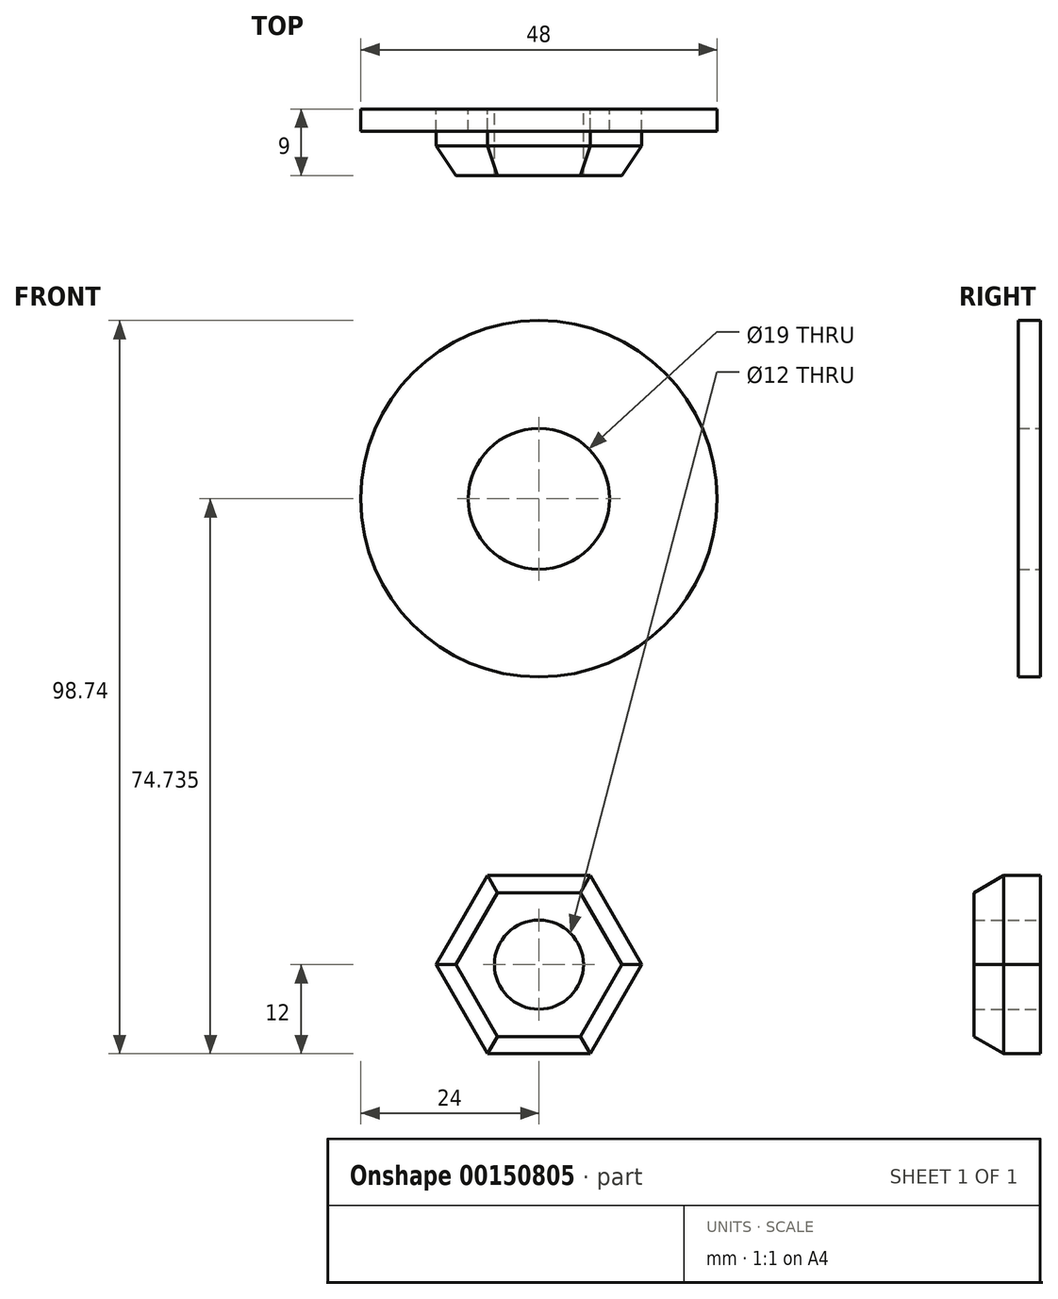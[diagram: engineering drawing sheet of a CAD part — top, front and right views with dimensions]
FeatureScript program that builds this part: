
annotation { "Feature Type Name" : "Feature", "Feature Type Description" : "" }
export const myFeature = defineFeature(function(context is Context, id is Id, definition is map)
    precondition{}
    {
        {
            var Q0;
            Q0=qCreatedBy(makeId("Front.planeOp"),FACE);
            var sketch = newSketch(context, id + "F0", { "sketchPlane" : qUnion([Q0])});
            skCircle(sketch, "E0.cCircle", {"center": v(0, 0) * mm, "radius": 12 * mm, "construction": true});
            skLineSegment(sketch, "E0.0", {"start": v(-6.93, 12) * mm, "end": v(6.93, 12) * mm});
            skLineSegment(sketch, "E0.1", {"start": v(6.93, 12) * mm, "end": v(13.86, 0) * mm});
            skLineSegment(sketch, "E0.2", {"start": v(13.86, 0) * mm, "end": v(6.93, -12) * mm});
            skLineSegment(sketch, "E0.3", {"start": v(6.93, -12) * mm, "end": v(-6.93, -12) * mm});
            skLineSegment(sketch, "E0.4", {"start": v(-6.93, -12) * mm, "end": v(-13.86, 0) * mm});
            skLineSegment(sketch, "E0.5", {"start": v(-13.86, 0) * mm, "end": v(-6.93, 12) * mm});
            skPoint(sketch, "E0.0.midPoint", {"position": v(0, 12) * mm});
            skCircle(sketch, "E1", {"center": v(0, 0) * mm, "radius": 6 * mm});
            skSolve(sketch);
        }
        {
            var Q0;
            Q0=qSketchRegion(id+"F0",true);
            extrude(context, id + "F1", {"entities" : qUnion([Q0]), "depth" : 9 * mm});
        }
        {
            var Q0;
            Q0=qCreatedBy(makeId("Front.planeOp"),FACE);
            var sketch = newSketch(context, id + "F2", { "sketchPlane" : qUnion([Q0])});
            skCircle(sketch, "E2", {"center": v(0, 62.74) * mm, "radius": 24 * mm});
            skCircle(sketch, "E3", {"center": v(0, 62.74) * mm, "radius": 9.5 * mm});
            skSolve(sketch);
        }
        {
            var Q0;
            Q0=makeQuery(id+"F2.imprint","IMPRINT",FACE,{"disambiguationData":[TD([[makeQuery(id+"F2.imprint","IMPRINT",EDGE,{"derivedFrom":sQuery(id+"F2.wireOp",EDGE,"E2")}),1.0]])]});
            extrude(context, id + "F3", {"entities" : qUnion([Q0]), "depth" : 3 * mm});
        }
        {
            var Q0;
            Q0=makeQuery(id+"F1.opExtrude","CAP_EDGE",EDGE,{"disambiguationData":[OSD([sQuery(id+"F0.wireOp",EDGE,"E0.4")])],"isStart":false});
            var Q1;
            Q1=makeQuery(id+"F1.opExtrude","CAP_EDGE",EDGE,{"disambiguationData":[OSD([sQuery(id+"F0.wireOp",EDGE,"E0.3")])],"isStart":false});
            var Q2;
            Q2=makeQuery(id+"F1.opExtrude","CAP_EDGE",EDGE,{"disambiguationData":[OSD([sQuery(id+"F0.wireOp",EDGE,"E0.2")])],"isStart":false});
            var Q3;
            Q3=makeQuery(id+"F1.opExtrude","CAP_EDGE",EDGE,{"disambiguationData":[OSD([sQuery(id+"F0.wireOp",EDGE,"E0.1")])],"isStart":false});
            var Q4;
            Q4=makeQuery(id+"F1.opExtrude","CAP_EDGE",EDGE,{"disambiguationData":[OSD([sQuery(id+"F0.wireOp",EDGE,"E0.0")])],"isStart":false});
            var Q5;
            Q5=makeQuery(id+"F1.opExtrude","CAP_EDGE",EDGE,{"disambiguationData":[OSD([sQuery(id+"F0.wireOp",EDGE,"E0.5")])],"isStart":false});
            chamfer(context, id + "F4", {"entities" : qUnion([Q0, Q1, Q2, Q3, Q4, Q5]), "chamferType" : ChamferType.OFFSET_ANGLE, "width" : 4 * mm, "oppositeDirection" : false, "angle" : 30 * degree, "tangentPropagation" : true});
        }
    });
